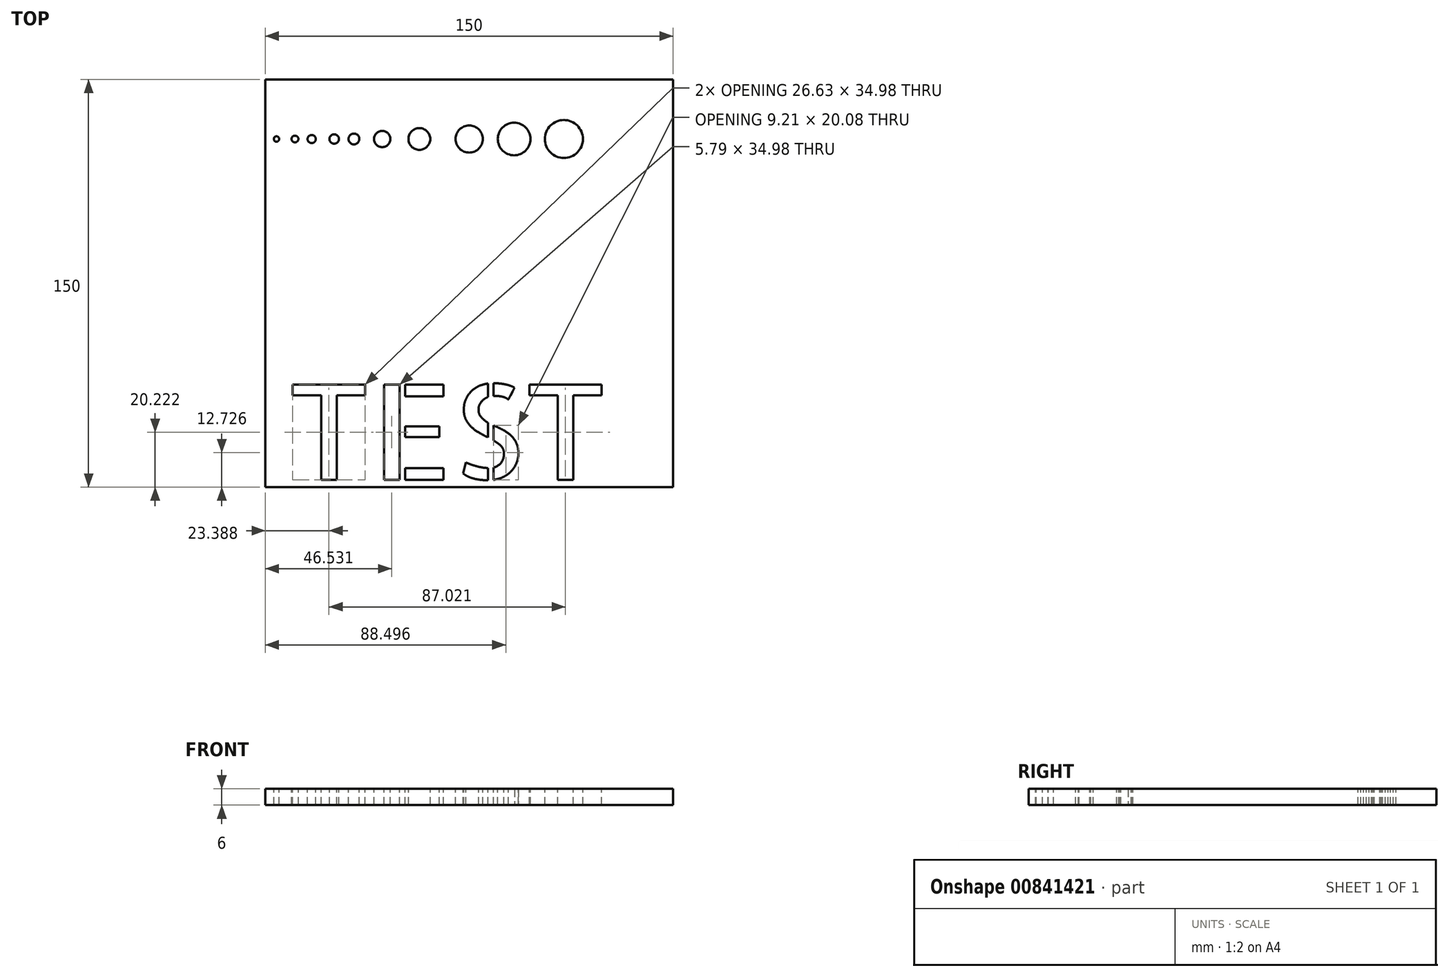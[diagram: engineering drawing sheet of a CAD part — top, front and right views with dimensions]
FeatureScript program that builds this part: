
annotation { "Feature Type Name" : "Feature", "Feature Type Description" : "" }
export const myFeature = defineFeature(function(context is Context, id is Id, definition is map)
    precondition{}
    {
        {
            var Q0;
            Q0=qCreatedBy(makeId("Top.planeOp"),FACE);
            var sketch = newSketch(context, id + "F0", { "sketchPlane" : qUnion([Q0])});
            skLineSegment(sketch, "E0.bottom", {"start": v(-75, 75) * mm, "end": v(75, 75) * mm});
            skLineSegment(sketch, "E0.top", {"start": v(-75, -75) * mm, "end": v(75, -75) * mm});
            skLineSegment(sketch, "E0.left", {"start": v(-75, 75) * mm, "end": v(-75, -75) * mm});
            skLineSegment(sketch, "E0.right", {"start": v(75, 75) * mm, "end": v(75, -75) * mm});
            skPoint(sketch, "E0.middle", {"position": v(0, 0) * mm});
            skSolve(sketch);
        }
        {
            var Q0;
            Q0=makeQuery(id+"F0.imprint","IMPRINT",FACE,{"disambiguationData":[TD([[makeQuery(id+"F0.imprint","IMPRINT",EDGE,{"derivedFrom":sQuery(id+"F0.wireOp",EDGE,"E0.bottom")}),-1.0]])]});
            extrude(context, id + "F1", {"entities" : qUnion([Q0]), "depth" : 6 * mm, "offsetDistance" : 25 * mm});
        }
        {
            var Q0;
            Q0=makeQuery(id+"F1.opExtrude","CAP_FACE",FACE,{"disambiguationData":[OSD([sQuery(id+"F0.wireOp",EDGE,"E0.bottom"),sQuery(id+"F0.wireOp",EDGE,"E0.top"),sQuery(id+"F0.wireOp",EDGE,"E0.left"),sQuery(id+"F0.wireOp",EDGE,"E0.right")])],"isStart":false});
            var sketch = newSketch(context, id + "F2", { "sketchPlane" : qUnion([Q0])});
            skLineSegment(sketch, "E1", {"start": v(-75, 53.11) * mm, "end": v(75, 53.11) * mm, "construction": true});
            skCircle(sketch, "E2", {"center": v(-70.88, 53.11) * mm, "radius": 1 * mm});
            skCircle(sketch, "E3", {"center": v(-64.1, 53.11) * mm, "radius": 1.25 * mm});
            skCircle(sketch, "E4", {"center": v(-57.95, 53.11) * mm, "radius": 1.5 * mm});
            skCircle(sketch, "E5", {"center": v(-49.68, 53.11) * mm, "radius": 1.75 * mm});
            skCircle(sketch, "E6", {"center": v(-42.4, 53.11) * mm, "radius": 2 * mm});
            skCircle(sketch, "E7", {"center": v(-32, 53.11) * mm, "radius": 3 * mm});
            skCircle(sketch, "E8", {"center": v(-18.33, 53.11) * mm, "radius": 4 * mm});
            skCircle(sketch, "E9", {"center": v(0, 53.11) * mm, "radius": 5 * mm});
            skCircle(sketch, "E10", {"center": v(16.52, 53.11) * mm, "radius": 6 * mm});
            skCircle(sketch, "E11", {"center": v(34.83, 53.11) * mm, "radius": 7 * mm});
            skSolve(sketch);
        }
        {
            var Q0;
            Q0=makeQuery(id+"F2.imprint","IMPRINT",FACE,{"disambiguationData":[TD([[makeQuery(id+"F2.imprint","IMPRINT",EDGE,{"derivedFrom":sQuery(id+"F2.wireOp",EDGE,"E10")}),1.0]])]});
            var Q1;
            Q1=makeQuery(id+"F2.imprint","IMPRINT",FACE,{"disambiguationData":[TD([[makeQuery(id+"F2.imprint","IMPRINT",EDGE,{"derivedFrom":sQuery(id+"F2.wireOp",EDGE,"E9")}),1.0]])]});
            var Q2;
            Q2=makeQuery(id+"F2.imprint","IMPRINT",FACE,{"disambiguationData":[TD([[makeQuery(id+"F2.imprint","IMPRINT",EDGE,{"derivedFrom":sQuery(id+"F2.wireOp",EDGE,"E8")}),1.0]])]});
            var Q3;
            Q3=makeQuery(id+"F2.imprint","IMPRINT",FACE,{"disambiguationData":[TD([[makeQuery(id+"F2.imprint","IMPRINT",EDGE,{"derivedFrom":sQuery(id+"F2.wireOp",EDGE,"E7")}),1.0]])]});
            var Q4;
            Q4=makeQuery(id+"F2.imprint","IMPRINT",FACE,{"disambiguationData":[TD([[makeQuery(id+"F2.imprint","IMPRINT",EDGE,{"derivedFrom":sQuery(id+"F2.wireOp",EDGE,"E11")}),1.0]])]});
            var Q5;
            Q5=makeQuery(id+"F2.imprint","IMPRINT",FACE,{"disambiguationData":[TD([[makeQuery(id+"F2.imprint","IMPRINT",EDGE,{"derivedFrom":sQuery(id+"F2.wireOp",EDGE,"E6")}),1.0]])]});
            var Q6;
            Q6=makeQuery(id+"F2.imprint","IMPRINT",FACE,{"disambiguationData":[TD([[makeQuery(id+"F2.imprint","IMPRINT",EDGE,{"derivedFrom":sQuery(id+"F2.wireOp",EDGE,"E5")}),1.0]])]});
            var Q7;
            Q7=makeQuery(id+"F2.imprint","IMPRINT",FACE,{"disambiguationData":[TD([[makeQuery(id+"F2.imprint","IMPRINT",EDGE,{"derivedFrom":sQuery(id+"F2.wireOp",EDGE,"E4")}),1.0]])]});
            var Q8;
            Q8=makeQuery(id+"F2.imprint","IMPRINT",FACE,{"disambiguationData":[TD([[makeQuery(id+"F2.imprint","IMPRINT",EDGE,{"derivedFrom":sQuery(id+"F2.wireOp",EDGE,"E3")}),1.0]])]});
            var Q9;
            Q9=makeQuery(id+"F2.imprint","IMPRINT",FACE,{"disambiguationData":[TD([[makeQuery(id+"F2.imprint","IMPRINT",EDGE,{"derivedFrom":sQuery(id+"F2.wireOp",EDGE,"E2")}),1.0]])]});
            extrude(context, id + "F3", {"entities" : qUnion([Q0, Q1, Q2, Q3, Q4, Q5, Q6, Q7, Q8, Q9]), "operationType" : NewBodyOperationType.REMOVE, "endBound" : BoundingType.THROUGH_ALL, "oppositeDirection" : true, "depth" : 25 * mm, "offsetDistance" : 25 * mm});
        }
        {
            var Q0;
            Q0=makeQuery(id+"F1.opExtrude","CAP_FACE",FACE,{"disambiguationData":[OSD([sQuery(id+"F0.wireOp",EDGE,"E0.bottom"),sQuery(id+"F0.wireOp",EDGE,"E0.top"),sQuery(id+"F0.wireOp",EDGE,"E0.left"),sQuery(id+"F0.wireOp",EDGE,"E0.right")])],"isStart":false});
            var sketch = newSketch(context, id + "F4", { "sketchPlane" : qUnion([Q0])});
            skText(sketch, "E12", { "text": "TEST", "fontName": "AllertaStencil-Regular.ttf"});
            const initialGuessF4  = {"E12": [-0.06735, -0.07227, 1, 0, 0.035]};
            skSetInitialGuess(sketch, initialGuessF4);
            skSolve(sketch);
        }
        {
            var Q0;
            Q0 = qSketchRegion(id + "F4", true);
            extrude(context, id + "F5", {"entities" : qUnion([Q0]), "operationType" : NewBodyOperationType.REMOVE, "oppositeDirection" : true, "depth" : 25 * mm, "offsetDistance" : 25 * mm});
        }
    });
